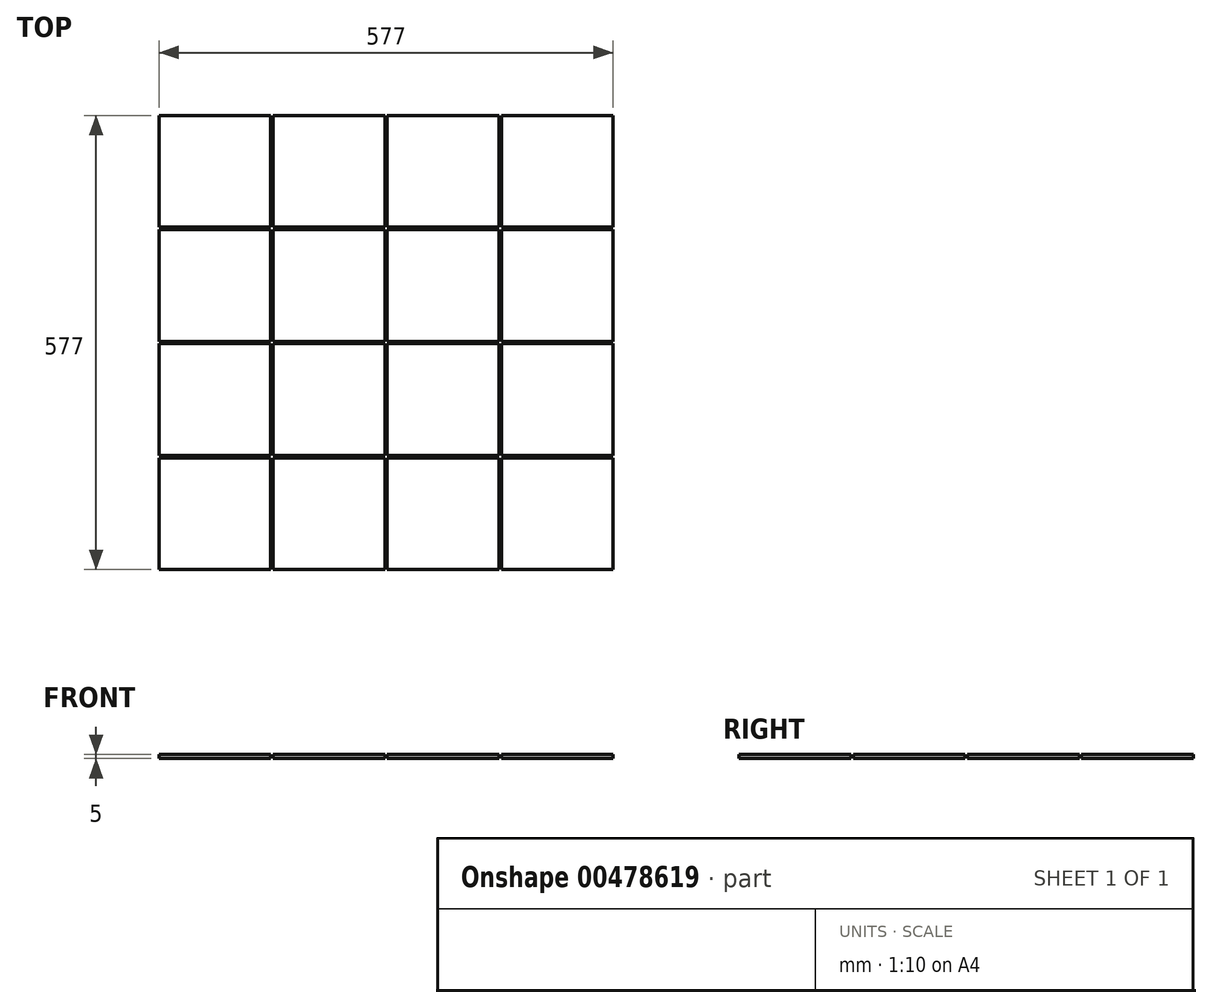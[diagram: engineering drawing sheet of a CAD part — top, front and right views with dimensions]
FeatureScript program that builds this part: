
annotation { "Feature Type Name" : "Feature", "Feature Type Description" : "" }
export const myFeature = defineFeature(function(context is Context, id is Id, definition is map)
    precondition{}
    {
        {
            var Q0;
            Q0=qCreatedBy(makeId("Top.planeOp"),FACE);
            var sketch = newSketch(context, id + "F0", { "sketchPlane" : qUnion([Q0])});
            skLineSegment(sketch, "E0.bottom", {"start": v(290, 290) * mm, "end": v(-290, 290) * mm});
            skLineSegment(sketch, "E0.top", {"start": v(290, -290) * mm, "end": v(-290, -290) * mm});
            skLineSegment(sketch, "E0.left", {"start": v(290, 290) * mm, "end": v(290, -290) * mm});
            skLineSegment(sketch, "E0.right", {"start": v(-290, 290) * mm, "end": v(-290, -290) * mm});
            skPoint(sketch, "E0.middle", {"position": v(0, 0) * mm});
            skLineSegment(sketch, "E1.bottom", {"start": v(-148, 148) * mm, "end": v(-290, 148) * mm});
            skLineSegment(sketch, "E1.top", {"start": v(-148, 290) * mm, "end": v(-290, 290) * mm});
            skLineSegment(sketch, "E1.left", {"start": v(-148, 148) * mm, "end": v(-148, 290) * mm});
            skLineSegment(sketch, "E1.right", {"start": v(-290, 148) * mm, "end": v(-290, 290) * mm});
            skPoint(sketch, "E1.middle", {"position": v(-219, 219) * mm});
            skLineSegment(sketch, "E2.0.1.0", {"start": v(-148, 3) * mm, "end": v(-148, 145) * mm});
            skLineSegment(sketch, "E2.0.1.1", {"start": v(-148, 145) * mm, "end": v(-290, 145) * mm});
            skLineSegment(sketch, "E2.0.1.2", {"start": v(-290, 3) * mm, "end": v(-290, 145) * mm});
            skLineSegment(sketch, "E2.0.1.3", {"start": v(-148, 3) * mm, "end": v(-290, 3) * mm});
            skPoint(sketch, "E2.0.1.4", {"position": v(-219, 74) * mm});
            skLineSegment(sketch, "E2.0.2.0", {"start": v(-148, -142) * mm, "end": v(-148, 0) * mm});
            skLineSegment(sketch, "E2.0.2.1", {"start": v(-148, 0) * mm, "end": v(-290, 0) * mm});
            skLineSegment(sketch, "E2.0.2.2", {"start": v(-290, -142) * mm, "end": v(-290, 0) * mm});
            skLineSegment(sketch, "E2.0.2.3", {"start": v(-148, -142) * mm, "end": v(-290, -142) * mm});
            skPoint(sketch, "E2.0.2.4", {"position": v(-219, -71) * mm});
            skLineSegment(sketch, "E2.0.3.0", {"start": v(-148, -287) * mm, "end": v(-148, -145) * mm});
            skLineSegment(sketch, "E2.0.3.1", {"start": v(-148, -145) * mm, "end": v(-290, -145) * mm});
            skLineSegment(sketch, "E2.0.3.2", {"start": v(-290, -287) * mm, "end": v(-290, -145) * mm});
            skLineSegment(sketch, "E2.0.3.3", {"start": v(-148, -287) * mm, "end": v(-290, -287) * mm});
            skPoint(sketch, "E2.0.3.4", {"position": v(-219, -216) * mm});
            skLineSegment(sketch, "E2.1.0.0", {"start": v(-3, 148) * mm, "end": v(-3, 290) * mm});
            skLineSegment(sketch, "E2.1.0.1", {"start": v(-3, 290) * mm, "end": v(-145, 290) * mm});
            skLineSegment(sketch, "E2.1.0.2", {"start": v(-145, 148) * mm, "end": v(-145, 290) * mm});
            skLineSegment(sketch, "E2.1.0.3", {"start": v(-3, 148) * mm, "end": v(-145, 148) * mm});
            skPoint(sketch, "E2.1.0.4", {"position": v(-74, 219) * mm});
            skLineSegment(sketch, "E2.1.1.0", {"start": v(-3, 3) * mm, "end": v(-3, 145) * mm});
            skLineSegment(sketch, "E2.1.1.1", {"start": v(-3, 145) * mm, "end": v(-145, 145) * mm});
            skLineSegment(sketch, "E2.1.1.2", {"start": v(-145, 3) * mm, "end": v(-145, 145) * mm});
            skLineSegment(sketch, "E2.1.1.3", {"start": v(-3, 3) * mm, "end": v(-145, 3) * mm});
            skPoint(sketch, "E2.1.1.4", {"position": v(-74, 74) * mm});
            skLineSegment(sketch, "E2.1.2.0", {"start": v(-3, -142) * mm, "end": v(-3, 0) * mm});
            skLineSegment(sketch, "E2.1.2.1", {"start": v(-3, 0) * mm, "end": v(-145, 0) * mm});
            skLineSegment(sketch, "E2.1.2.2", {"start": v(-145, -142) * mm, "end": v(-145, 0) * mm});
            skLineSegment(sketch, "E2.1.2.3", {"start": v(-3, -142) * mm, "end": v(-145, -142) * mm});
            skPoint(sketch, "E2.1.2.4", {"position": v(-74, -71) * mm});
            skLineSegment(sketch, "E2.1.3.0", {"start": v(-3, -287) * mm, "end": v(-3, -145) * mm});
            skLineSegment(sketch, "E2.1.3.1", {"start": v(-3, -145) * mm, "end": v(-145, -145) * mm});
            skLineSegment(sketch, "E2.1.3.2", {"start": v(-145, -287) * mm, "end": v(-145, -145) * mm});
            skLineSegment(sketch, "E2.1.3.3", {"start": v(-3, -287) * mm, "end": v(-145, -287) * mm});
            skPoint(sketch, "E2.1.3.4", {"position": v(-74, -216) * mm});
            skLineSegment(sketch, "E2.2.0.0", {"start": v(142, 148) * mm, "end": v(142, 290) * mm});
            skLineSegment(sketch, "E2.2.0.1", {"start": v(142, 290) * mm, "end": v(0, 290) * mm});
            skLineSegment(sketch, "E2.2.0.2", {"start": v(0, 148) * mm, "end": v(0, 290) * mm});
            skLineSegment(sketch, "E2.2.0.3", {"start": v(142, 148) * mm, "end": v(0, 148) * mm});
            skPoint(sketch, "E2.2.0.4", {"position": v(71, 219) * mm});
            skLineSegment(sketch, "E2.2.1.0", {"start": v(142, 3) * mm, "end": v(142, 145) * mm});
            skLineSegment(sketch, "E2.2.1.1", {"start": v(142, 145) * mm, "end": v(0, 145) * mm});
            skLineSegment(sketch, "E2.2.1.2", {"start": v(0, 3) * mm, "end": v(0, 145) * mm});
            skLineSegment(sketch, "E2.2.1.3", {"start": v(142, 3) * mm, "end": v(0, 3) * mm});
            skPoint(sketch, "E2.2.1.4", {"position": v(71, 74) * mm});
            skLineSegment(sketch, "E2.2.2.0", {"start": v(142, -142) * mm, "end": v(142, 0) * mm});
            skLineSegment(sketch, "E2.2.2.1", {"start": v(142, 0) * mm, "end": v(0, 0) * mm});
            skLineSegment(sketch, "E2.2.2.2", {"start": v(0, -142) * mm, "end": v(0, 0) * mm});
            skLineSegment(sketch, "E2.2.2.3", {"start": v(142, -142) * mm, "end": v(0, -142) * mm});
            skPoint(sketch, "E2.2.2.4", {"position": v(71, -71) * mm});
            skLineSegment(sketch, "E2.2.3.0", {"start": v(142, -287) * mm, "end": v(142, -145) * mm});
            skLineSegment(sketch, "E2.2.3.1", {"start": v(142, -145) * mm, "end": v(0, -145) * mm});
            skLineSegment(sketch, "E2.2.3.2", {"start": v(0, -287) * mm, "end": v(0, -145) * mm});
            skLineSegment(sketch, "E2.2.3.3", {"start": v(142, -287) * mm, "end": v(0, -287) * mm});
            skPoint(sketch, "E2.2.3.4", {"position": v(71, -216) * mm});
            skLineSegment(sketch, "E2.3.0.0", {"start": v(287, 148) * mm, "end": v(287, 290) * mm});
            skLineSegment(sketch, "E2.3.0.1", {"start": v(287, 290) * mm, "end": v(145, 290) * mm});
            skLineSegment(sketch, "E2.3.0.2", {"start": v(145, 148) * mm, "end": v(145, 290) * mm});
            skLineSegment(sketch, "E2.3.0.3", {"start": v(287, 148) * mm, "end": v(145, 148) * mm});
            skPoint(sketch, "E2.3.0.4", {"position": v(216, 219) * mm});
            skLineSegment(sketch, "E2.3.1.0", {"start": v(287, 3) * mm, "end": v(287, 145) * mm});
            skLineSegment(sketch, "E2.3.1.1", {"start": v(287, 145) * mm, "end": v(145, 145) * mm});
            skLineSegment(sketch, "E2.3.1.2", {"start": v(145, 3) * mm, "end": v(145, 145) * mm});
            skLineSegment(sketch, "E2.3.1.3", {"start": v(287, 3) * mm, "end": v(145, 3) * mm});
            skPoint(sketch, "E2.3.1.4", {"position": v(216, 74) * mm});
            skLineSegment(sketch, "E2.3.2.0", {"start": v(287, -142) * mm, "end": v(287, 0) * mm});
            skLineSegment(sketch, "E2.3.2.1", {"start": v(287, 0) * mm, "end": v(145, 0) * mm});
            skLineSegment(sketch, "E2.3.2.2", {"start": v(145, -142) * mm, "end": v(145, 0) * mm});
            skLineSegment(sketch, "E2.3.2.3", {"start": v(287, -142) * mm, "end": v(145, -142) * mm});
            skPoint(sketch, "E2.3.2.4", {"position": v(216, -71) * mm});
            skLineSegment(sketch, "E2.3.3.0", {"start": v(287, -287) * mm, "end": v(287, -145) * mm});
            skLineSegment(sketch, "E2.3.3.1", {"start": v(287, -145) * mm, "end": v(145, -145) * mm});
            skLineSegment(sketch, "E2.3.3.2", {"start": v(145, -287) * mm, "end": v(145, -145) * mm});
            skLineSegment(sketch, "E2.3.3.3", {"start": v(287, -287) * mm, "end": v(145, -287) * mm});
            skPoint(sketch, "E2.3.3.4", {"position": v(216, -216) * mm});
            skLineSegment(sketch, "E2.direction1", {"start": v(-148, 148) * mm, "end": v(-3, 148) * mm, "construction": true});
            skLineSegment(sketch, "E2.direction2", {"start": v(-148, 148) * mm, "end": v(-148, 3) * mm, "construction": true});
            skSolve(sketch);
        }
        {
            var Q0;
            Q0=makeQuery(id+"F0.imprint","IMPRINT",FACE,{"disambiguationData":[TD([[makeQuery(id+"F0.imprint","IMPRINT",EDGE,{"derivedFrom":sQuery(id+"F0.wireOp",EDGE,"fd7a4af9-2ca9-45bc-8ed5-d687ac33fcd5.0.0.7")}),1.0]])]});
            var Q1;
            Q1=makeQuery(id+"F0.imprint","IMPRINT",FACE,{"disambiguationData":[TD([[makeQuery(id+"F0.imprint","IMPRINT",EDGE,{"derivedFrom":sQuery(id+"F0.wireOp",EDGE,"fd7a4af9-2ca9-45bc-8ed5-d687ac33fcd5.0.0.6")}),1.0]])]});
            var Q2;
            Q2=makeQuery(id+"F0.imprint","IMPRINT",FACE,{"disambiguationData":[TD([[makeQuery(id+"F0.imprint","IMPRINT",EDGE,{"derivedFrom":sQuery(id+"F0.wireOp",EDGE,"E2.0.5.0")}),1.0]])]});
            var Q3;
            Q3=makeQuery(id+"F0.imprint","IMPRINT",FACE,{"disambiguationData":[TD([[makeQuery(id+"F0.imprint","IMPRINT",EDGE,{"derivedFrom":sQuery(id+"F0.wireOp",EDGE,"E2.0.4.0")}),1.0]])]});
            var Q4;
            Q4=makeQuery(id+"F0.imprint","IMPRINT",FACE,{"disambiguationData":[TD([[makeQuery(id+"F0.imprint","IMPRINT",EDGE,{"derivedFrom":sQuery(id+"F0.wireOp",EDGE,"E2.0.3.0")}),1.0]])]});
            var Q5;
            Q5=makeQuery(id+"F0.imprint","IMPRINT",FACE,{"disambiguationData":[TD([[makeQuery(id+"F0.imprint","IMPRINT",EDGE,{"derivedFrom":sQuery(id+"F0.wireOp",EDGE,"E2.0.2.0")}),1.0]])]});
            var Q6;
            Q6=makeQuery(id+"F0.imprint","IMPRINT",FACE,{"disambiguationData":[TD([[makeQuery(id+"F0.imprint","IMPRINT",EDGE,{"derivedFrom":sQuery(id+"F0.wireOp",EDGE,"E2.0.1.0")}),1.0]])]});
            var Q7;
            Q7=makeQuery(id+"F0.imprint","IMPRINT",FACE,{"disambiguationData":[TD([[makeQuery(id+"F0.imprint","IMPRINT",EDGE,{"derivedFrom":sQuery(id+"F0.wireOp",EDGE,"E1.bottom")}),-1.0]])]});
            var Q8;
            Q8=makeQuery(id+"F0.imprint","IMPRINT",FACE,{"disambiguationData":[TD([[makeQuery(id+"F0.imprint","IMPRINT",EDGE,{"derivedFrom":sQuery(id+"F0.wireOp",EDGE,"E2.1.0.0")}),1.0]])]});
            var Q9;
            Q9=makeQuery(id+"F0.imprint","IMPRINT",FACE,{"disambiguationData":[TD([[makeQuery(id+"F0.imprint","IMPRINT",EDGE,{"derivedFrom":sQuery(id+"F0.wireOp",EDGE,"E2.2.0.0")}),1.0]])]});
            var Q10;
            Q10=makeQuery(id+"F0.imprint","IMPRINT",FACE,{"disambiguationData":[TD([[makeQuery(id+"F0.imprint","IMPRINT",EDGE,{"derivedFrom":sQuery(id+"F0.wireOp",EDGE,"E2.3.0.0")}),1.0]])]});
            var Q11;
            Q11=makeQuery(id+"F0.imprint","IMPRINT",FACE,{"disambiguationData":[TD([[makeQuery(id+"F0.imprint","IMPRINT",EDGE,{"derivedFrom":sQuery(id+"F0.wireOp",EDGE,"E2.4.0.0")}),1.0]])]});
            var Q12;
            Q12=makeQuery(id+"F0.imprint","IMPRINT",FACE,{"disambiguationData":[TD([[makeQuery(id+"F0.imprint","IMPRINT",EDGE,{"derivedFrom":sQuery(id+"F0.wireOp",EDGE,"acd5cf0f-649e-495b-8dc7-9b612795613a.0.6.0")}),1.0]])]});
            var Q13;
            Q13=makeQuery(id+"F0.imprint","IMPRINT",FACE,{"disambiguationData":[TD([[makeQuery(id+"F0.imprint","IMPRINT",EDGE,{"derivedFrom":sQuery(id+"F0.wireOp",EDGE,"E2.5.0.0")}),1.0]])]});
            var Q14;
            Q14=makeQuery(id+"F0.imprint","IMPRINT",FACE,{"disambiguationData":[TD([[makeQuery(id+"F0.imprint","IMPRINT",EDGE,{"derivedFrom":sQuery(id+"F0.wireOp",EDGE,"acd5cf0f-649e-495b-8dc7-9b612795613a.0.7.0")}),1.0]])]});
            var Q15;
            Q15=makeQuery(id+"F0.imprint","IMPRINT",FACE,{"disambiguationData":[TD([[makeQuery(id+"F0.imprint","IMPRINT",EDGE,{"derivedFrom":sQuery(id+"F0.wireOp",EDGE,"acd5cf0f-649e-495b-8dc7-9b612795613a.0.7.1")}),1.0]])]});
            var Q16;
            Q16=makeQuery(id+"F0.imprint","IMPRINT",FACE,{"disambiguationData":[TD([[makeQuery(id+"F0.imprint","IMPRINT",EDGE,{"derivedFrom":sQuery(id+"F0.wireOp",EDGE,"acd5cf0f-649e-495b-8dc7-9b612795613a.0.7.2")}),1.0]])]});
            var Q17;
            Q17=makeQuery(id+"F0.imprint","IMPRINT",FACE,{"disambiguationData":[TD([[makeQuery(id+"F0.imprint","IMPRINT",EDGE,{"derivedFrom":sQuery(id+"F0.wireOp",EDGE,"acd5cf0f-649e-495b-8dc7-9b612795613a.0.6.2")}),1.0]])]});
            var Q18;
            Q18=makeQuery(id+"F0.imprint","IMPRINT",FACE,{"disambiguationData":[TD([[makeQuery(id+"F0.imprint","IMPRINT",EDGE,{"derivedFrom":sQuery(id+"F0.wireOp",EDGE,"E2.5.2.0")}),1.0]])]});
            var Q19;
            Q19=makeQuery(id+"F0.imprint","IMPRINT",FACE,{"disambiguationData":[TD([[makeQuery(id+"F0.imprint","IMPRINT",EDGE,{"derivedFrom":sQuery(id+"F0.wireOp",EDGE,"E2.4.2.0")}),1.0]])]});
            var Q20;
            Q20=makeQuery(id+"F0.imprint","IMPRINT",FACE,{"disambiguationData":[TD([[makeQuery(id+"F0.imprint","IMPRINT",EDGE,{"derivedFrom":sQuery(id+"F0.wireOp",EDGE,"E2.3.2.0")}),1.0]])]});
            var Q21;
            Q21=makeQuery(id+"F0.imprint","IMPRINT",FACE,{"disambiguationData":[TD([[makeQuery(id+"F0.imprint","IMPRINT",EDGE,{"derivedFrom":sQuery(id+"F0.wireOp",EDGE,"E2.2.2.0")}),1.0]])]});
            var Q22;
            Q22=makeQuery(id+"F0.imprint","IMPRINT",FACE,{"disambiguationData":[TD([[makeQuery(id+"F0.imprint","IMPRINT",EDGE,{"derivedFrom":sQuery(id+"F0.wireOp",EDGE,"E2.2.3.0")}),1.0]])]});
            var Q23;
            Q23=makeQuery(id+"F0.imprint","IMPRINT",FACE,{"disambiguationData":[TD([[makeQuery(id+"F0.imprint","IMPRINT",EDGE,{"derivedFrom":sQuery(id+"F0.wireOp",EDGE,"E2.3.3.0")}),1.0]])]});
            var Q24;
            Q24=makeQuery(id+"F0.imprint","IMPRINT",FACE,{"disambiguationData":[TD([[makeQuery(id+"F0.imprint","IMPRINT",EDGE,{"derivedFrom":sQuery(id+"F0.wireOp",EDGE,"E2.4.3.0")}),1.0]])]});
            var Q25;
            Q25=makeQuery(id+"F0.imprint","IMPRINT",FACE,{"disambiguationData":[TD([[makeQuery(id+"F0.imprint","IMPRINT",EDGE,{"derivedFrom":sQuery(id+"F0.wireOp",EDGE,"E2.5.3.0")}),1.0]])]});
            var Q26;
            Q26=makeQuery(id+"F0.imprint","IMPRINT",FACE,{"disambiguationData":[TD([[makeQuery(id+"F0.imprint","IMPRINT",EDGE,{"derivedFrom":sQuery(id+"F0.wireOp",EDGE,"acd5cf0f-649e-495b-8dc7-9b612795613a.0.6.3")}),1.0]])]});
            var Q27;
            Q27=makeQuery(id+"F0.imprint","IMPRINT",FACE,{"disambiguationData":[TD([[makeQuery(id+"F0.imprint","IMPRINT",EDGE,{"derivedFrom":sQuery(id+"F0.wireOp",EDGE,"acd5cf0f-649e-495b-8dc7-9b612795613a.0.7.4")}),1.0]])]});
            var Q28;
            Q28=makeQuery(id+"F0.imprint","IMPRINT",FACE,{"disambiguationData":[TD([[makeQuery(id+"F0.imprint","IMPRINT",EDGE,{"derivedFrom":sQuery(id+"F0.wireOp",EDGE,"acd5cf0f-649e-495b-8dc7-9b612795613a.0.6.4")}),1.0]])]});
            var Q29;
            Q29=makeQuery(id+"F0.imprint","IMPRINT",FACE,{"disambiguationData":[TD([[makeQuery(id+"F0.imprint","IMPRINT",EDGE,{"derivedFrom":sQuery(id+"F0.wireOp",EDGE,"E2.5.4.0")}),1.0]])]});
            var Q30;
            Q30=makeQuery(id+"F0.imprint","IMPRINT",FACE,{"disambiguationData":[TD([[makeQuery(id+"F0.imprint","IMPRINT",EDGE,{"derivedFrom":sQuery(id+"F0.wireOp",EDGE,"E2.4.4.0")}),1.0]])]});
            var Q31;
            Q31=makeQuery(id+"F0.imprint","IMPRINT",FACE,{"disambiguationData":[TD([[makeQuery(id+"F0.imprint","IMPRINT",EDGE,{"derivedFrom":sQuery(id+"F0.wireOp",EDGE,"E2.3.4.0")}),1.0]])]});
            var Q32;
            Q32=makeQuery(id+"F0.imprint","IMPRINT",FACE,{"disambiguationData":[TD([[makeQuery(id+"F0.imprint","IMPRINT",EDGE,{"derivedFrom":sQuery(id+"F0.wireOp",EDGE,"acd5cf0f-649e-495b-8dc7-9b612795613a.0.7.3")}),1.0]])]});
            var Q33;
            Q33=makeQuery(id+"F0.imprint","IMPRINT",FACE,{"disambiguationData":[TD([[makeQuery(id+"F0.imprint","IMPRINT",EDGE,{"derivedFrom":sQuery(id+"F0.wireOp",EDGE,"E2.4.1.0")}),1.0]])]});
            var Q34;
            Q34=makeQuery(id+"F0.imprint","IMPRINT",FACE,{"disambiguationData":[TD([[makeQuery(id+"F0.imprint","IMPRINT",EDGE,{"derivedFrom":sQuery(id+"F0.wireOp",EDGE,"E2.5.1.0")}),1.0]])]});
            var Q35;
            Q35=makeQuery(id+"F0.imprint","IMPRINT",FACE,{"disambiguationData":[TD([[makeQuery(id+"F0.imprint","IMPRINT",EDGE,{"derivedFrom":sQuery(id+"F0.wireOp",EDGE,"acd5cf0f-649e-495b-8dc7-9b612795613a.0.6.1")}),1.0]])]});
            var Q36;
            Q36=makeQuery(id+"F0.imprint","IMPRINT",FACE,{"disambiguationData":[TD([[makeQuery(id+"F0.imprint","IMPRINT",EDGE,{"derivedFrom":sQuery(id+"F0.wireOp",EDGE,"E2.3.1.0")}),1.0]])]});
            var Q37;
            Q37=makeQuery(id+"F0.imprint","IMPRINT",FACE,{"disambiguationData":[TD([[makeQuery(id+"F0.imprint","IMPRINT",EDGE,{"derivedFrom":sQuery(id+"F0.wireOp",EDGE,"E2.2.1.0")}),1.0]])]});
            var Q38;
            Q38=makeQuery(id+"F0.imprint","IMPRINT",FACE,{"disambiguationData":[TD([[makeQuery(id+"F0.imprint","IMPRINT",EDGE,{"derivedFrom":sQuery(id+"F0.wireOp",EDGE,"E2.1.1.0")}),1.0]])]});
            var Q39;
            Q39=makeQuery(id+"F0.imprint","IMPRINT",FACE,{"disambiguationData":[TD([[makeQuery(id+"F0.imprint","IMPRINT",EDGE,{"derivedFrom":sQuery(id+"F0.wireOp",EDGE,"E2.1.2.0")}),1.0]])]});
            var Q40;
            Q40=makeQuery(id+"F0.imprint","IMPRINT",FACE,{"disambiguationData":[TD([[makeQuery(id+"F0.imprint","IMPRINT",EDGE,{"derivedFrom":sQuery(id+"F0.wireOp",EDGE,"E2.1.3.0")}),1.0]])]});
            var Q41;
            Q41=makeQuery(id+"F0.imprint","IMPRINT",FACE,{"disambiguationData":[TD([[makeQuery(id+"F0.imprint","IMPRINT",EDGE,{"derivedFrom":sQuery(id+"F0.wireOp",EDGE,"E2.1.4.0")}),1.0]])]});
            var Q42;
            Q42=makeQuery(id+"F0.imprint","IMPRINT",FACE,{"disambiguationData":[TD([[makeQuery(id+"F0.imprint","IMPRINT",EDGE,{"derivedFrom":sQuery(id+"F0.wireOp",EDGE,"E2.2.4.0")}),1.0]])]});
            var Q43;
            Q43=makeQuery(id+"F0.imprint","IMPRINT",FACE,{"disambiguationData":[TD([[makeQuery(id+"F0.imprint","IMPRINT",EDGE,{"derivedFrom":sQuery(id+"F0.wireOp",EDGE,"E2.1.5.0")}),1.0]])]});
            var Q44;
            Q44=makeQuery(id+"F0.imprint","IMPRINT",FACE,{"disambiguationData":[TD([[makeQuery(id+"F0.imprint","IMPRINT",EDGE,{"derivedFrom":sQuery(id+"F0.wireOp",EDGE,"E2.2.5.0")}),1.0]])]});
            var Q45;
            Q45=makeQuery(id+"F0.imprint","IMPRINT",FACE,{"disambiguationData":[TD([[makeQuery(id+"F0.imprint","IMPRINT",EDGE,{"derivedFrom":sQuery(id+"F0.wireOp",EDGE,"E2.3.5.0")}),1.0]])]});
            var Q46;
            Q46=makeQuery(id+"F0.imprint","IMPRINT",FACE,{"disambiguationData":[TD([[makeQuery(id+"F0.imprint","IMPRINT",EDGE,{"derivedFrom":sQuery(id+"F0.wireOp",EDGE,"E2.4.5.0")}),1.0]])]});
            var Q47;
            Q47=makeQuery(id+"F0.imprint","IMPRINT",FACE,{"disambiguationData":[TD([[makeQuery(id+"F0.imprint","IMPRINT",EDGE,{"derivedFrom":sQuery(id+"F0.wireOp",EDGE,"E2.5.5.0")}),1.0]])]});
            var Q48;
            Q48=makeQuery(id+"F0.imprint","IMPRINT",FACE,{"disambiguationData":[TD([[makeQuery(id+"F0.imprint","IMPRINT",EDGE,{"derivedFrom":sQuery(id+"F0.wireOp",EDGE,"acd5cf0f-649e-495b-8dc7-9b612795613a.0.6.5")}),1.0]])]});
            var Q49;
            Q49=makeQuery(id+"F0.imprint","IMPRINT",FACE,{"disambiguationData":[TD([[makeQuery(id+"F0.imprint","IMPRINT",EDGE,{"derivedFrom":sQuery(id+"F0.wireOp",EDGE,"acd5cf0f-649e-495b-8dc7-9b612795613a.0.7.5")}),1.0]])]});
            var Q50;
            Q50=makeQuery(id+"F0.imprint","IMPRINT",FACE,{"disambiguationData":[TD([[makeQuery(id+"F0.imprint","IMPRINT",EDGE,{"derivedFrom":sQuery(id+"F0.wireOp",EDGE,"acd5cf0f-649e-495b-8dc7-9b612795613a.0.7.6")}),1.0]])]});
            var Q51;
            Q51=makeQuery(id+"F0.imprint","IMPRINT",FACE,{"disambiguationData":[TD([[makeQuery(id+"F0.imprint","IMPRINT",EDGE,{"derivedFrom":sQuery(id+"F0.wireOp",EDGE,"acd5cf0f-649e-495b-8dc7-9b612795613a.0.6.6")}),1.0]])]});
            var Q52;
            Q52=makeQuery(id+"F0.imprint","IMPRINT",FACE,{"disambiguationData":[TD([[makeQuery(id+"F0.imprint","IMPRINT",EDGE,{"derivedFrom":sQuery(id+"F0.wireOp",EDGE,"fd7a4af9-2ca9-45bc-8ed5-d687ac33fcd5.0.5.6")}),1.0]])]});
            var Q53;
            Q53=makeQuery(id+"F0.imprint","IMPRINT",FACE,{"disambiguationData":[TD([[makeQuery(id+"F0.imprint","IMPRINT",EDGE,{"derivedFrom":sQuery(id+"F0.wireOp",EDGE,"fd7a4af9-2ca9-45bc-8ed5-d687ac33fcd5.0.4.6")}),1.0]])]});
            var Q54;
            Q54=makeQuery(id+"F0.imprint","IMPRINT",FACE,{"disambiguationData":[TD([[makeQuery(id+"F0.imprint","IMPRINT",EDGE,{"derivedFrom":sQuery(id+"F0.wireOp",EDGE,"fd7a4af9-2ca9-45bc-8ed5-d687ac33fcd5.0.3.6")}),1.0]])]});
            var Q55;
            Q55=makeQuery(id+"F0.imprint","IMPRINT",FACE,{"disambiguationData":[TD([[makeQuery(id+"F0.imprint","IMPRINT",EDGE,{"derivedFrom":sQuery(id+"F0.wireOp",EDGE,"fd7a4af9-2ca9-45bc-8ed5-d687ac33fcd5.0.2.6")}),1.0]])]});
            var Q56;
            Q56=makeQuery(id+"F0.imprint","IMPRINT",FACE,{"disambiguationData":[TD([[makeQuery(id+"F0.imprint","IMPRINT",EDGE,{"derivedFrom":sQuery(id+"F0.wireOp",EDGE,"fd7a4af9-2ca9-45bc-8ed5-d687ac33fcd5.0.1.6")}),1.0]])]});
            var Q57;
            Q57=makeQuery(id+"F0.imprint","IMPRINT",FACE,{"disambiguationData":[TD([[makeQuery(id+"F0.imprint","IMPRINT",EDGE,{"derivedFrom":sQuery(id+"F0.wireOp",EDGE,"fd7a4af9-2ca9-45bc-8ed5-d687ac33fcd5.0.3.7")}),1.0]])]});
            var Q58;
            Q58=makeQuery(id+"F0.imprint","IMPRINT",FACE,{"disambiguationData":[TD([[makeQuery(id+"F0.imprint","IMPRINT",EDGE,{"derivedFrom":sQuery(id+"F0.wireOp",EDGE,"fd7a4af9-2ca9-45bc-8ed5-d687ac33fcd5.0.4.7")}),1.0]])]});
            var Q59;
            Q59=makeQuery(id+"F0.imprint","IMPRINT",FACE,{"disambiguationData":[TD([[makeQuery(id+"F0.imprint","IMPRINT",EDGE,{"derivedFrom":sQuery(id+"F0.wireOp",EDGE,"fd7a4af9-2ca9-45bc-8ed5-d687ac33fcd5.0.5.7")}),1.0]])]});
            var Q60;
            Q60=makeQuery(id+"F0.imprint","IMPRINT",FACE,{"disambiguationData":[TD([[makeQuery(id+"F0.imprint","IMPRINT",EDGE,{"derivedFrom":sQuery(id+"F0.wireOp",EDGE,"acd5cf0f-649e-495b-8dc7-9b612795613a.0.6.7")}),1.0]])]});
            var Q61;
            Q61=makeQuery(id+"F0.imprint","IMPRINT",FACE,{"disambiguationData":[TD([[makeQuery(id+"F0.imprint","IMPRINT",EDGE,{"derivedFrom":sQuery(id+"F0.wireOp",EDGE,"fd7a4af9-2ca9-45bc-8ed5-d687ac33fcd5.0.1.7")}),1.0]])]});
            var Q62;
            Q62=makeQuery(id+"F0.imprint","IMPRINT",FACE,{"disambiguationData":[TD([[makeQuery(id+"F0.imprint","IMPRINT",EDGE,{"derivedFrom":sQuery(id+"F0.wireOp",EDGE,"fd7a4af9-2ca9-45bc-8ed5-d687ac33fcd5.0.2.7")}),1.0]])]});
            var Q63;
            Q63=makeQuery(id+"F0.imprint","IMPRINT",FACE,{"disambiguationData":[TD([[makeQuery(id+"F0.imprint","IMPRINT",EDGE,{"derivedFrom":sQuery(id+"F0.wireOp",EDGE,"acd5cf0f-649e-495b-8dc7-9b612795613a.0.7.7")}),1.0]])]});
            extrude(context, id + "F1", {"entities" : qUnion([Q0, Q1, Q2, Q3, Q4, Q5, Q6, Q7, Q8, Q9, Q10, Q11, Q12, Q13, Q14, Q15, Q16, Q17, Q18, Q19, Q20, Q21, Q22, Q23, Q24, Q25, Q26, Q27, Q28, Q29, Q30, Q31, Q32, Q33, Q34, Q35, Q36, Q37, Q38, Q39, Q40, Q41, Q42, Q43, Q44, Q45, Q46, Q47, Q48, Q49, Q50, Q51, Q52, Q53, Q54, Q55, Q56, Q57, Q58, Q59, Q60, Q61, Q62, Q63]), "depth" : 5 * mm, "offsetDistance" : 25 * mm});
        }
    });
